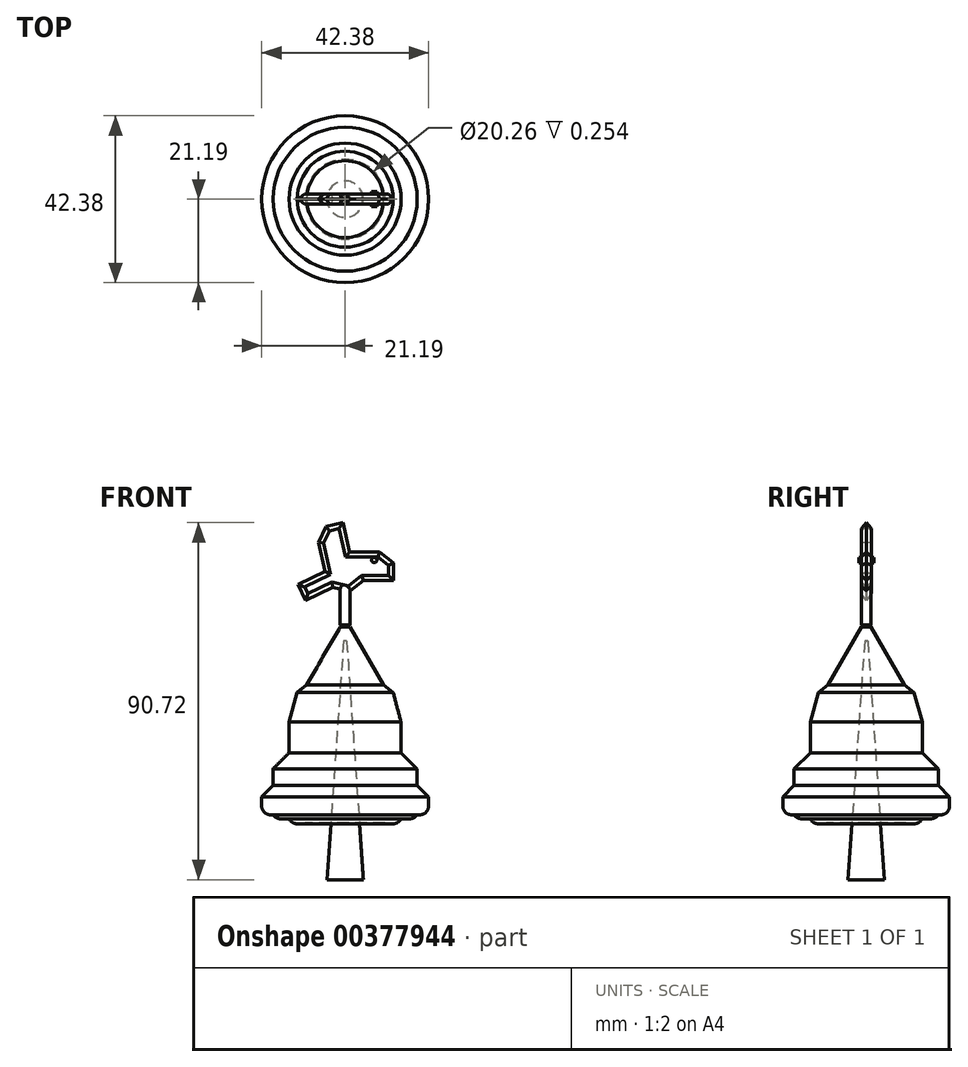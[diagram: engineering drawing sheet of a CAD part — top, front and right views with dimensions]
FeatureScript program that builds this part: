
annotation { "Feature Type Name" : "Feature", "Feature Type Description" : "" }
export const myFeature = defineFeature(function(context is Context, id is Id, definition is map)
    precondition{}
    {
        {
            var Q0;
            Q0=qCreatedBy(makeId("Top.planeOp"),FACE);
            var sketch = newSketch(context, id + "F0", { "sketchPlane" : qUnion([Q0])});
            skCircle(sketch, "E0", {"center": v(0, 0) * mm, "radius": 5.47 * mm});
            skCircle(sketch, "E1", {"center": v(0, 0) * mm, "radius": 21.2 * mm});
            skCircle(sketch, "E2", {"center": v(0, 0) * mm, "radius": 18.3 * mm});
            skCircle(sketch, "E3", {"center": v(0, 0) * mm, "radius": 14.22 * mm});
            skCircle(sketch, "E4", {"center": v(0, 0) * mm, "radius": 10.13 * mm});
            skSolve(sketch);
        }
        {
            var Q0;
            Q0=makeQuery(id+"F0.imprint","IMPRINT",FACE,{"disambiguationData":[TD([[makeQuery(id+"F0.imprint","IMPRINT",EDGE,{"derivedFrom":sQuery(id+"F0.wireOp",EDGE,"E0")}),1.0]])]});
            extrude(context, id + "F1", {"entities" : qUnion([Q0]), "depth" : 60.7 * mm});
        }
        {
            var Q0;
            Q0=makeQuery(id+"F1.opExtrude","CAP_EDGE",EDGE,{"disambiguationData":[OSD([sQuery(id+"F0.wireOp",EDGE,"E0")])],"isStart":false});
            chamfer(context, id + "F2", {"entities" : qUnion([Q0]), "chamferType" : ChamferType.OFFSET_ANGLE, "width" : 5.08 * mm, "oppositeDirection" : false, "angle" : 86 * degree, "tangentPropagation" : true});
        }
        {
            var Q0;
            Q0=makeQuery(id+"F0.imprint","IMPRINT",FACE,{"disambiguationData":[TD([[makeQuery(id+"F0.imprint","IMPRINT",EDGE,{"derivedFrom":sQuery(id+"F0.wireOp",EDGE,"E0")}),-1.0]])]});
            var Q1;
            Q1=makeQuery(id+"F0.imprint","IMPRINT",FACE,{"disambiguationData":[TD([[makeQuery(id+"F0.imprint","IMPRINT",EDGE,{"derivedFrom":sQuery(id+"F0.wireOp",EDGE,"E0")}),1.0]])]});
            extrude(context, id + "F3", {"entities" : qUnion([Q0, Q1]), "depth" : 64.26 * mm, "hasSecondDirection" : true, "secondDirectionOppositeDirection" : false, "secondDirectionDepth" : 14.48 * mm});
        }
        {
            var Q0;
            Q0=makeQuery(id+"F0.imprint","IMPRINT",FACE,{"disambiguationData":[TD([[makeQuery(id+"F0.imprint","IMPRINT",EDGE,{"derivedFrom":sQuery(id+"F0.wireOp",EDGE,"E3")}),1.0]])]});
            extrude(context, id + "F4", {"entities" : qUnion([Q0]), "operationType" : NewBodyOperationType.ADD, "depth" : 49.53 * mm, "hasSecondDirection" : true, "secondDirectionOppositeDirection" : false, "secondDirectionDepth" : 14.22 * mm});
        }
        {
            var Q0;
            Q0=makeQuery(id+"F0.imprint","IMPRINT",FACE,{"disambiguationData":[TD([[makeQuery(id+"F0.imprint","IMPRINT",EDGE,{"derivedFrom":sQuery(id+"F0.wireOp",EDGE,"E2")}),1.0]])]});
            extrude(context, id + "F5", {"entities" : qUnion([Q0]), "operationType" : NewBodyOperationType.ADD, "depth" : 33.27 * mm, "hasSecondDirection" : true, "secondDirectionOppositeDirection" : false, "secondDirectionDepth" : 15.5 * mm});
        }
        {
            var Q0;
            Q0=makeQuery(id+"F0.imprint","IMPRINT",FACE,{"disambiguationData":[TD([[makeQuery(id+"F0.imprint","IMPRINT",EDGE,{"derivedFrom":sQuery(id+"F0.wireOp",EDGE,"E1")}),1.0]])]});
            extrude(context, id + "F6", {"entities" : qUnion([Q0]), "operationType" : NewBodyOperationType.ADD, "depth" : 26.16 * mm, "hasSecondDirection" : true, "secondDirectionOppositeDirection" : false, "secondDirectionDepth" : 16.5 * mm});
        }
        {
            var Q0;
            Q0=makeQuery(id+"F3.opExtrude","CAP_EDGE",EDGE,{"disambiguationData":[OSD([sQuery(id+"F0.wireOp",EDGE,"E4")])],"isStart":false});
            chamfer(context, id + "F7", {"entities" : qUnion([Q0]), "chamferType" : ChamferType.OFFSET_ANGLE, "width" : 8.9 * mm, "oppositeDirection" : false, "angle" : 60 * degree, "tangentPropagation" : true});
        }
        {
            var Q0;
            Q0=makeQuery(id+"F4.opExtrude","CAP_EDGE",EDGE,{"disambiguationData":[OSD([sQuery(id+"F0.wireOp",EDGE,"E3")])],"isStart":false});
            chamfer(context, id + "F8", {"entities" : qUnion([Q0]), "chamferType" : ChamferType.OFFSET_ANGLE, "width" : 2.54 * mm, "oppositeDirection" : false, "angle" : 75 * degree, "tangentPropagation" : true});
        }
        {
            var Q0;
            Q0=makeQuery(id+"F5.opExtrude","CAP_EDGE",EDGE,{"disambiguationData":[OSD([sQuery(id+"F0.wireOp",EDGE,"E2")])],"isStart":false});
            var Q1;
            Q1=makeQuery(id+"F6.opExtrude","CAP_EDGE",EDGE,{"disambiguationData":[OSD([sQuery(id+"F0.wireOp",EDGE,"E1")])],"isStart":false});
            chamfer(context, id + "F9", {"entities" : qUnion([Q0, Q1]), "width" : 5.08 * mm, "tangentPropagation" : true});
        }
        {
            var Q0;
            Q0=makeQuery(id+"F6.opExtrude","CAP_EDGE",EDGE,{"disambiguationData":[OSD([sQuery(id+"F0.wireOp",EDGE,"E1")])],"isStart":true});
            var Q1;
            Q1=makeQuery(id+"F5.opExtrude","CAP_EDGE",EDGE,{"disambiguationData":[OSD([sQuery(id+"F0.wireOp",EDGE,"E2")])],"isStart":true});
            var Q2;
            Q2=makeQuery(id+"F4.opExtrude","CAP_EDGE",EDGE,{"disambiguationData":[OSD([sQuery(id+"F0.wireOp",EDGE,"E3")])],"isStart":true});
            fillet(context, id + "F10", {"entities" : qUnion([Q0, Q1, Q2]), "radius" : 2.2 * mm, "tangentPropagation" : true, "allowEdgeOverflow" : false});
        }
        {
            var Q0;
            {var subQ0=sQuery(id+"F0.wireOp",EDGE,"E3");Q0=makeQuery(id+"F8.opChamfer","BLEND_EDGE",EDGE,{"blendedFrom":[makeQuery(id+"F4.opExtrude","CAP_EDGE",EDGE,{"disambiguationData":[OSD([subQ0])],"isStart":false}),makeQuery(id+"F4.opExtrude","CAP_FACE",FACE,{"disambiguationData":[OSD([subQ0,sQuery(id+"F0.wireOp",EDGE,"E4")])],"isStart":false})],"blendedInto":[makeQuery(id+"F4.opExtrude","CAP_FACE",FACE,{"disambiguationData":[OSD([subQ0,sQuery(id+"F0.wireOp",EDGE,"E4")])],"isStart":false})]});}
            chamfer(context, id + "F11", {"entities" : qUnion([Q0]), "width" : 2.54 * mm, "tangentPropagation" : true});
        }
        {
            var Q0;
            Q0=makeQuery(id+"F3.opExtrude","CAP_FACE",FACE,{"disambiguationData":[OSD([sQuery(id+"F0.wireOp",EDGE,"E4")])],"isStart":false});
            extrude(context, id + "F12", {"entities" : qUnion([Q0]), "depth" : 15 * mm});
        }
        {
            var Q0;
            Q0=makeQuery(id+"F12.opExtrude","SWEPT_FACE",FACE,{"disambiguationData":[OSD([sQuery(id+"F0.wireOp",EDGE,"E4")])]});
            chamfer(context, id + "F13", {"entities" : qUnion([Q0]), "chamferType" : ChamferType.OFFSET_ANGLE, "width" : 0.5 * mm, "oppositeDirection" : true, "angle" : 45 * degree, "tangentPropagation" : true});
        }
        {
            var Q0;
            Q0=qCreatedBy(makeId("Front.planeOp"),FACE);
            var sketch = newSketch(context, id + "F14", { "sketchPlane" : qUnion([Q0])});
            skCircle(sketch, "E5.cCircle", {"center": v(0, 78.3) * mm, "radius": 4.61 * mm, "construction": true});
            skLineSegment(sketch, "E5.0", {"start": v(4.61, 80.52) * mm, "end": v(4.61, 76.08) * mm});
            skLineSegment(sketch, "E5.1", {"start": v(4.61, 76.08) * mm, "end": v(1.14, 73.3) * mm});
            skLineSegment(sketch, "E5.2", {"start": v(1.14, 73.3) * mm, "end": v(-3.2, 74.3) * mm});
            skLineSegment(sketch, "E5.3", {"start": v(-3.2, 74.3) * mm, "end": v(-5.12, 78.3) * mm});
            skLineSegment(sketch, "E5.4", {"start": v(-5.12, 78.3) * mm, "end": v(-3.2, 82.3) * mm});
            skLineSegment(sketch, "E5.5", {"start": v(-3.2, 82.3) * mm, "end": v(1.14, 83.29) * mm});
            skLineSegment(sketch, "E5.6", {"start": v(1.14, 83.29) * mm, "end": v(4.61, 80.52) * mm});
            skPoint(sketch, "E5.0.midPoint", {"position": v(4.61, 78.3) * mm});
            skCircle(sketch, "E6", {"center": v(7.4, 81.2) * mm, "radius": 0.66 * mm});
            skSolve(sketch);
        }
        {
            var Q0;
            Q0=makeQuery(id+"F14.imprint","IMPRINT",FACE,{"disambiguationData":[TD([[makeQuery(id+"F14.imprint","IMPRINT",EDGE,{"derivedFrom":sQuery(id+"F14.wireOp",EDGE,"E5.0")}),-1.0]])]});
            extrude(context, id + "F15", {"entities" : qUnion([Q0]), "operationType" : NewBodyOperationType.ADD, "endBound" : BoundingType.SYMMETRIC, "depth" : 2.54 * mm});
        }
        {
            var Q0;
            Q0=makeQuery(id+"F15.opExtrude","SWEPT_FACE",FACE,{"disambiguationData":[OSD([sQuery(id+"F14.wireOp",EDGE,"E5.5")])]});
            var Q1;
            Q1=makeQuery(id+"F15.opExtrude","SWEPT_FACE",FACE,{"disambiguationData":[OSD([sQuery(id+"F14.wireOp",EDGE,"E5.4")])]});
            extrude(context, id + "F16", {"entities" : qUnion([Q0, Q1]), "operationType" : NewBodyOperationType.ADD, "depth" : 7.62 * mm});
        }
        {
            var Q0;
            Q0=makeQuery(id+"F15.opExtrude","SWEPT_FACE",FACE,{"disambiguationData":[OSD([sQuery(id+"F14.wireOp",EDGE,"E5.0")])]});
            var Q1;
            Q1=makeQuery(id+"F15.opExtrude","SWEPT_FACE",FACE,{"disambiguationData":[OSD([sQuery(id+"F14.wireOp",EDGE,"E5.6")])]});
            extrude(context, id + "F17", {"entities" : qUnion([Q0, Q1]), "operationType" : NewBodyOperationType.ADD, "depth" : 7.62 * mm});
        }
        {
            var Q0;
            Q0=makeQuery(id+"F15.opExtrude","SWEPT_FACE",FACE,{"disambiguationData":[OSD([sQuery(id+"F14.wireOp",EDGE,"E5.3")])]});
            extrude(context, id + "F18", {"entities" : qUnion([Q0]), "operationType" : NewBodyOperationType.ADD, "depth" : 7.62 * mm});
        }
        {
            var Q0;
            {var subQ0=sQuery(id+"F14.wireOp",EDGE,"E5.3");var subQ1=sQuery(id+"F14.wireOp",EDGE,"E5.0");var subQ2=sQuery(id+"F14.wireOp",EDGE,"E5.5");Q0=makeQuery(id+"F18.boolean.opBoolean","MERGE",FACE,{"derivedFrom":[makeQuery(id+"F17.boolean.opBoolean","MERGE",FACE,{"derivedFrom":[makeQuery(id+"F16.boolean.opBoolean","MERGE",FACE,{"derivedFrom":[makeQuery(id+"F15.opExtrude","CAP_FACE",FACE,{"disambiguationData":[OSD([subQ1,sQuery(id+"F14.wireOp",EDGE,"E5.1"),sQuery(id+"F14.wireOp",EDGE,"E5.2"),subQ0,sQuery(id+"F14.wireOp",EDGE,"E5.4"),subQ2,sQuery(id+"F14.wireOp",EDGE,"E5.6")])],"isStart":true}),makeQuery(id+"F16.opExtrude","SWEPT_FACE",FACE,{"disambiguationData":[OSD([subQ2]),TDD([makeQuery(id+"F15.opExtrude","CAP_EDGE",EDGE,{"disambiguationData":[OSD([subQ2])],"isStart":true})])]})]}),makeQuery(id+"F17.opExtrude","SWEPT_FACE",FACE,{"disambiguationData":[OSD([subQ1]),TDD([makeQuery(id+"F15.opExtrude","CAP_EDGE",EDGE,{"disambiguationData":[OSD([subQ1])],"isStart":true})])]})]}),makeQuery(id+"F18.opExtrude","SWEPT_FACE",FACE,{"disambiguationData":[OSD([subQ0]),TDD([makeQuery(id+"F15.opExtrude","CAP_EDGE",EDGE,{"disambiguationData":[OSD([subQ0])],"isStart":true})])]})]});}
            var Q1;
            {var subQ0=sQuery(id+"F14.wireOp",EDGE,"E5.3");var subQ1=sQuery(id+"F14.wireOp",EDGE,"E5.0");var subQ2=sQuery(id+"F14.wireOp",EDGE,"E5.5");Q1=makeQuery(id+"F18.boolean.opBoolean","MERGE",FACE,{"derivedFrom":[makeQuery(id+"F17.boolean.opBoolean","MERGE",FACE,{"derivedFrom":[makeQuery(id+"F16.boolean.opBoolean","MERGE",FACE,{"derivedFrom":[makeQuery(id+"F15.opExtrude","CAP_FACE",FACE,{"disambiguationData":[OSD([subQ1,sQuery(id+"F14.wireOp",EDGE,"E5.1"),sQuery(id+"F14.wireOp",EDGE,"E5.2"),subQ0,sQuery(id+"F14.wireOp",EDGE,"E5.4"),subQ2,sQuery(id+"F14.wireOp",EDGE,"E5.6")])],"isStart":false}),makeQuery(id+"F16.opExtrude","SWEPT_FACE",FACE,{"disambiguationData":[OSD([subQ2]),TDD([makeQuery(id+"F15.opExtrude","CAP_EDGE",EDGE,{"disambiguationData":[OSD([subQ2])],"isStart":false})])]})]}),makeQuery(id+"F17.opExtrude","SWEPT_FACE",FACE,{"disambiguationData":[OSD([subQ1]),TDD([makeQuery(id+"F15.opExtrude","CAP_EDGE",EDGE,{"disambiguationData":[OSD([subQ1])],"isStart":false})])]})]}),makeQuery(id+"F18.opExtrude","SWEPT_FACE",FACE,{"disambiguationData":[OSD([subQ0]),TDD([makeQuery(id+"F15.opExtrude","CAP_EDGE",EDGE,{"disambiguationData":[OSD([subQ0])],"isStart":false})])]})]});}
            chamfer(context, id + "F19", {"entities" : qUnion([Q0, Q1]), "width" : 1.27 * mm, "tangentPropagation" : true});
        }
        {
            var Q0;
            Q0=makeQuery(id+"F14.imprint","IMPRINT",FACE,{"disambiguationData":[TD([[makeQuery(id+"F14.imprint","IMPRINT",EDGE,{"derivedFrom":sQuery(id+"F14.wireOp",EDGE,"E6")}),1.0]])]});
            extrude(context, id + "F20", {"entities" : qUnion([Q0]), "operationType" : NewBodyOperationType.ADD, "endBound" : BoundingType.SYMMETRIC, "depth" : 3.8 * mm});
        }
    });
